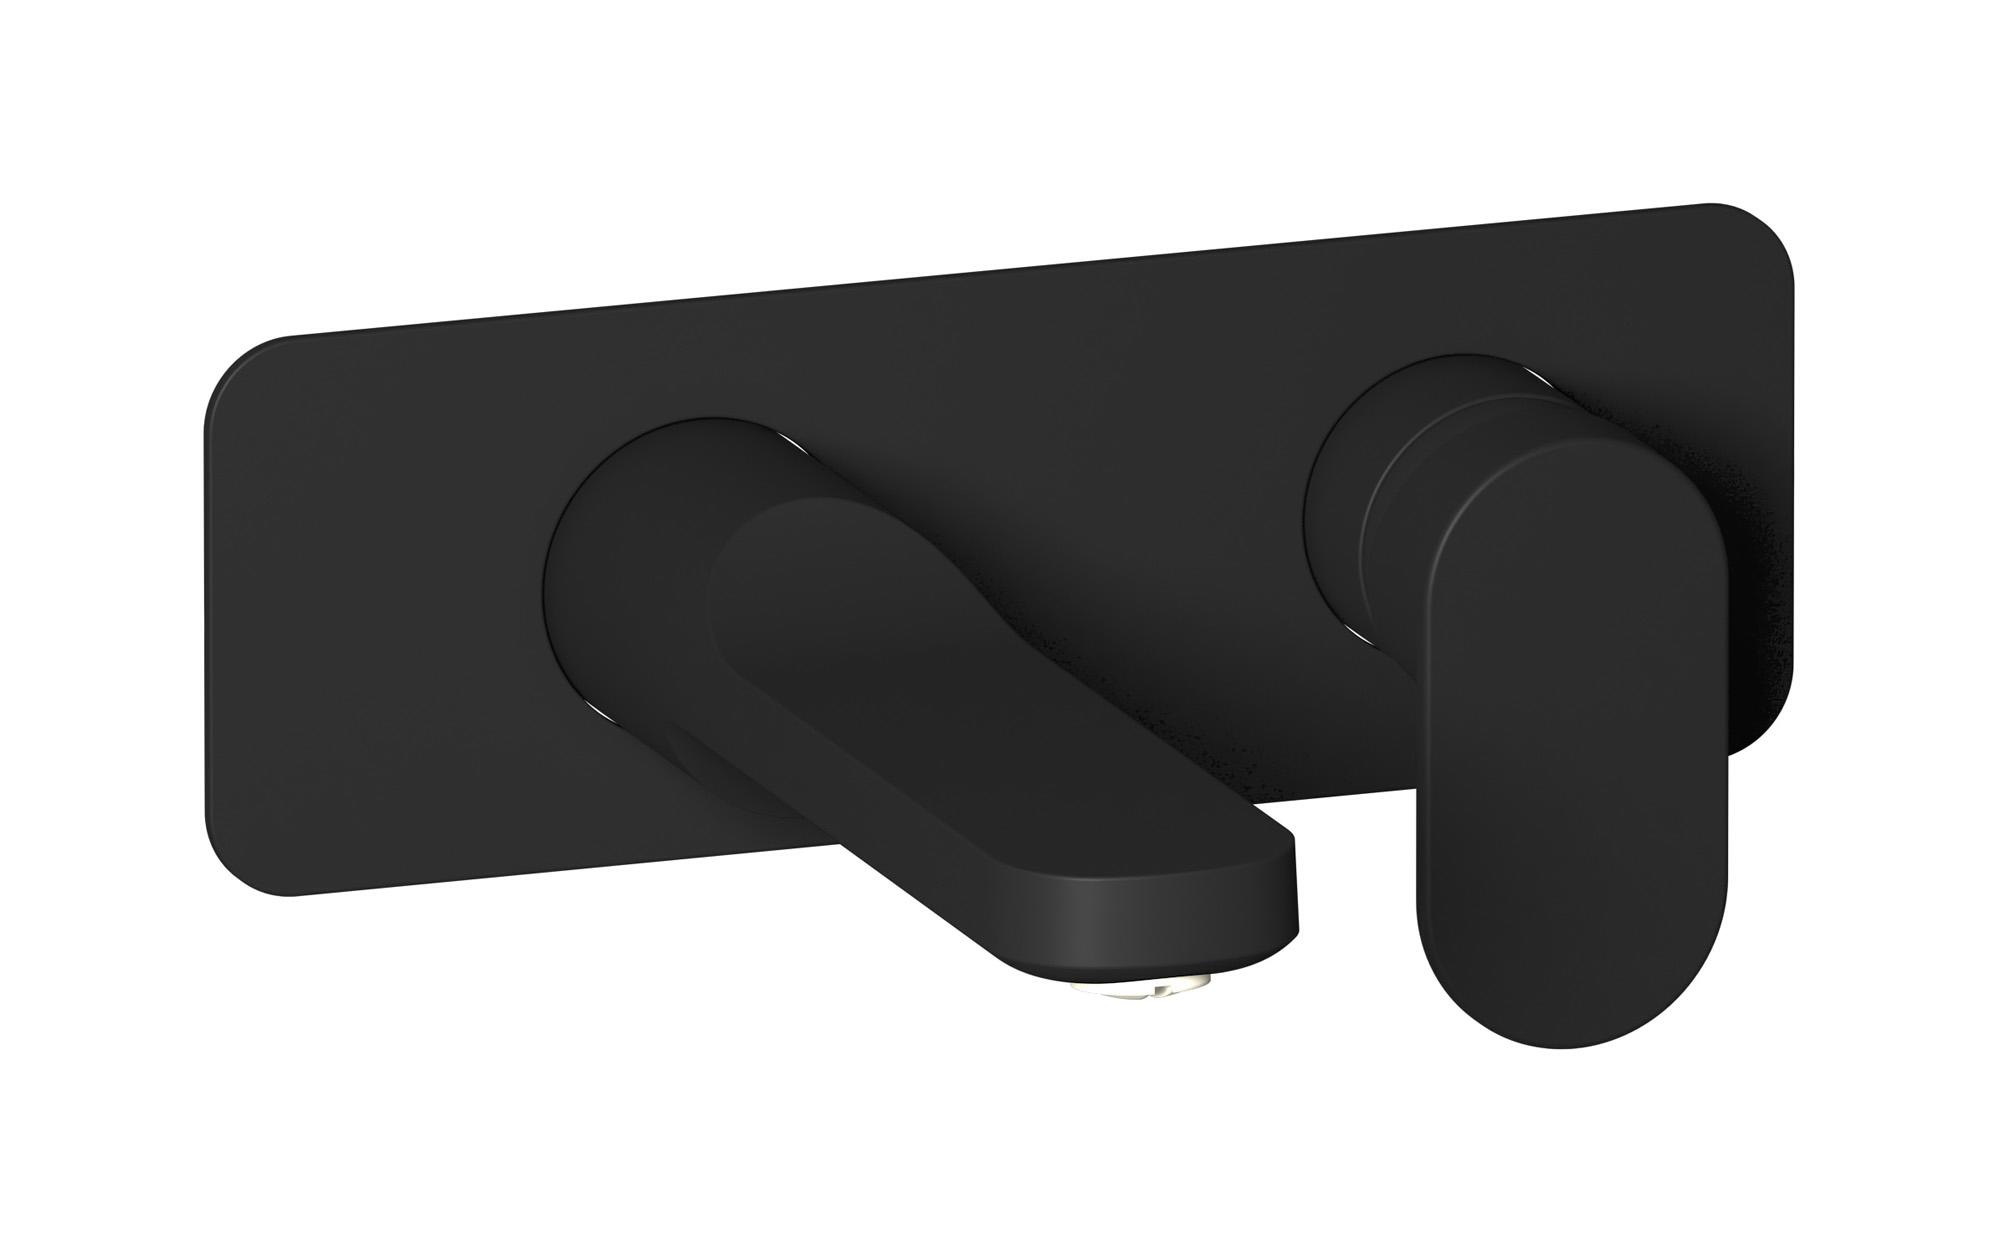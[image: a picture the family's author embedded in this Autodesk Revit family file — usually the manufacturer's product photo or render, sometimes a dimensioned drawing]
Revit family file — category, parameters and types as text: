
# Revit family: YP206
name_source: partatom
category: Apparecchi idraulici
units: mm (PartAtom-declared; Revit-internal decimal feet)

## family parameters
Basato su piano di lavoro = No
Condiviso = No
Mantieni orientamento annotazione = No
Numero OmniClass = 23.45.55.17
Punto di calcolo locali = No
Quota connettore circolare = Usa diametro
Sempre verticale = Sì
Taglio con vuoti quando caricato = No
Tipo di parte = Normale
Titolo OmniClass = Mixing Faucets

## types (2) — shared parameters
Cold water inlet = 10 mm  [stored 0.0328084 ft]
Commenti sul tipo = Wall mounted washbasin mixer complete with drain
Connessione CW = No
Connessione HW = No
Connessione di scarico = No
Connessione di ventilazione = No
Descrizione = Wall mounted washbasin mixer complete with drain
Hot water inlet = 10 mm  [stored 0.0328084 ft]
Produttore = IB Rubinetterie S.p.A.
URL = https://www.weareib.it
zero-valued in all types: Prospetto di default

## per-type parameters (varying)
| type | Finishes surface | Immagine tipo | Modello |
| Chrome | IB_Chrome | YP206CC.jpg | YP206CC |
| Matt Black | IB_matt black | YP206NP.jpg | YP206NP |

note: [stored X ft] marks values corroborated as IEEE doubles in the binary element streams (Revit-internal decimal feet)
